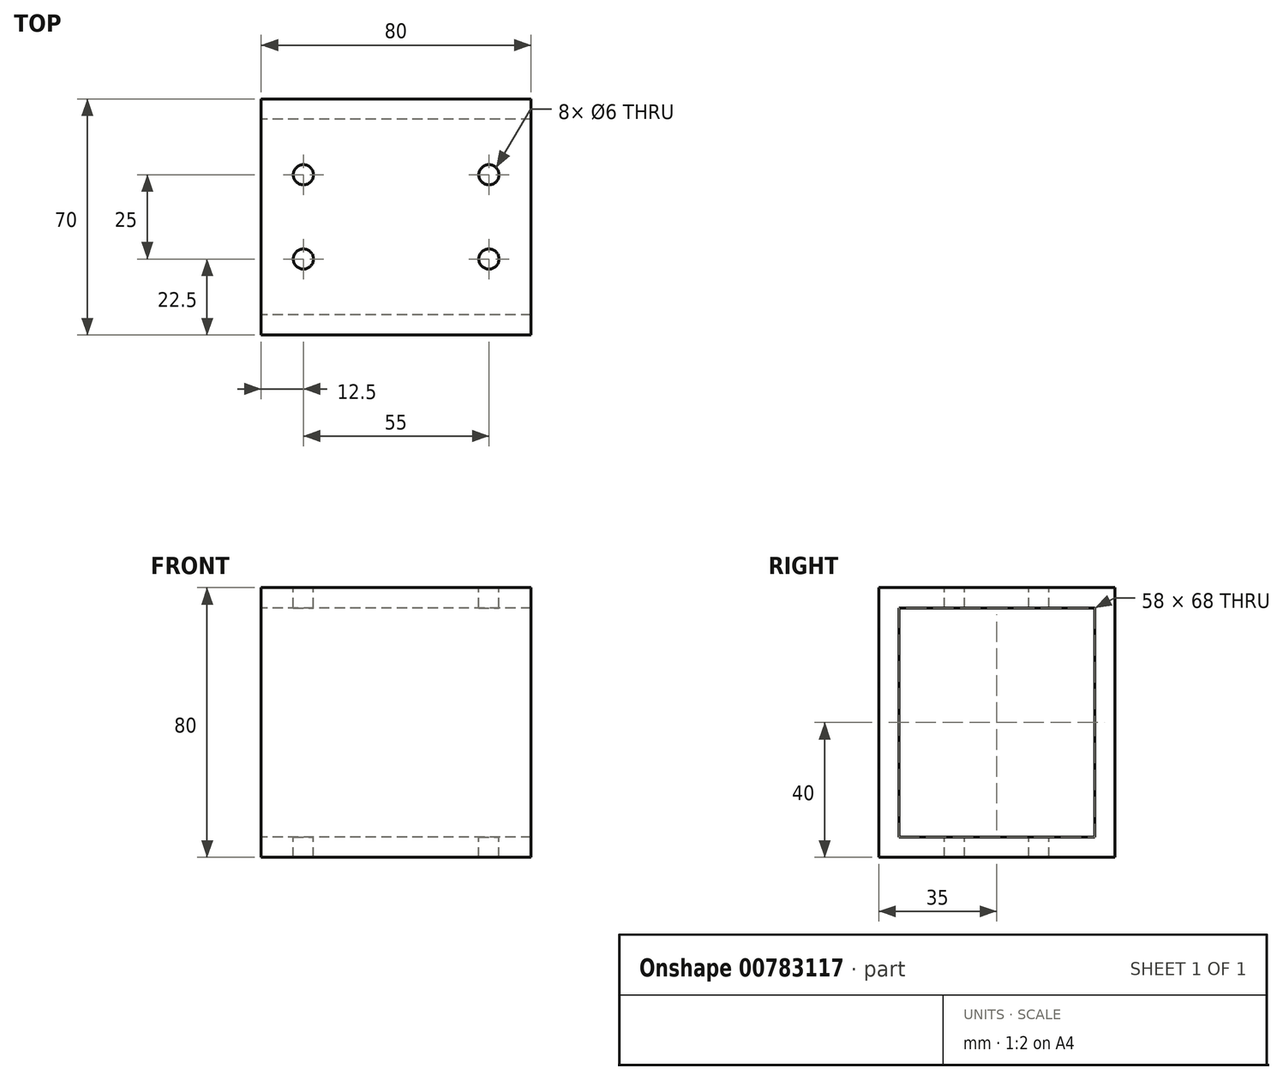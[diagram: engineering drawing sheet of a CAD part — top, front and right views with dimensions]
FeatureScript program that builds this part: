
annotation { "Feature Type Name" : "Feature", "Feature Type Description" : "" }
export const myFeature = defineFeature(function(context is Context, id is Id, definition is map)
    precondition{}
    {
        {
            var Q0;
            Q0=qCreatedBy(makeId("Right.planeOp"),FACE);
            var sketch = newSketch(context, id + "F0", { "sketchPlane" : qUnion([Q0])});
            skLineSegment(sketch, "E0.bottom", {"start": v(0, 0) * mm, "end": v(-70, 0) * mm});
            skLineSegment(sketch, "E0.top", {"start": v(0, 80) * mm, "end": v(-70, 80) * mm});
            skLineSegment(sketch, "E0.left", {"start": v(0, 0) * mm, "end": v(0, 80) * mm});
            skLineSegment(sketch, "E0.right", {"start": v(-70, 0) * mm, "end": v(-70, 80) * mm});
            skLineSegment(sketch, "E1.0", {"start": v(-6, 74) * mm, "end": v(-64, 74) * mm});
            skLineSegment(sketch, "E1.1", {"start": v(-6, 6) * mm, "end": v(-6, 74) * mm});
            skLineSegment(sketch, "E1.2", {"start": v(-6, 6) * mm, "end": v(-64, 6) * mm});
            skLineSegment(sketch, "E1.3", {"start": v(-64, 6) * mm, "end": v(-64, 74) * mm});
            skSolve(sketch);
        }
        {
            var Q0;
            Q0=makeQuery(id+"F0.imprint","IMPRINT",FACE,{"disambiguationData":[TD([[makeQuery(id+"F0.imprint","IMPRINT",EDGE,{"derivedFrom":sQuery(id+"F0.wireOp",EDGE,"E0.bottom")}),-1.0]])]});
            extrude(context, id + "F1", {"entities" : qUnion([Q0]), "depth" : 80 * mm, "offsetDistance" : 25 * mm});
        }
        {
            var Q0;
            Q0=makeQuery(id+"F1.opExtrude","SWEPT_FACE",FACE,{"disambiguationData":[OSD([sQuery(id+"F0.wireOp",EDGE,"E0.top")])]});
            var sketch = newSketch(context, id + "F2", { "sketchPlane" : qUnion([Q0])});
            skCircle(sketch, "E2", {"center": v(12.5, -22.5) * mm, "radius": 2.05 * mm});
            skCircle(sketch, "E3", {"center": v(67.5, -22.5) * mm, "radius": 2.05 * mm});
            skCircle(sketch, "E4", {"center": v(12.5, -47.5) * mm, "radius": 3.8 * mm});
            skCircle(sketch, "E5", {"center": v(67.5, -47.5) * mm, "radius": 2.54 * mm});
            skSolve(sketch);
        }
        {
            var Q0;
            Q0=sQuery(id+"F2.wireOp",VERTEX,"E2.center");
            var Q1;
            Q1=sQuery(id+"F2.wireOp",VERTEX,"E3.center");
            var Q2;
            Q2=sQuery(id+"F2.wireOp",VERTEX,"E5.center");
            var Q3;
            Q3=sQuery(id+"F2.wireOp",VERTEX,"E4.center");
            var Q4;
            Q4=makeQuery(id+"F1.opExtrude","SWEPT_BODY",BODY,{"disambiguationData":[OSD([sQuery(id+"F0.wireOp",EDGE,"E0.bottom"),sQuery(id+"F0.wireOp",EDGE,"E0.top"),sQuery(id+"F0.wireOp",EDGE,"E0.left"),sQuery(id+"F0.wireOp",EDGE,"E0.right"),sQuery(id+"F0.wireOp",EDGE,"E1.0"),sQuery(id+"F0.wireOp",EDGE,"E1.1"),sQuery(id+"F0.wireOp",EDGE,"E1.2"),sQuery(id+"F0.wireOp",EDGE,"E1.3")])]});
            hole(context, id + "F3", {"style" : HoleStyle.SIMPLE, "endStyle" : HoleEndStyle.THROUGH, "holeDiameter" : 6 * mm, "majorDiameter" : 5 * mm, "isTappedThrough" : true, "tappedDepth" : 12 * mm, "tapClearance" : 3, "locations" : qUnion([Q0, Q1, Q2, Q3]), "scope" : qUnion([Q4])});
        }
    });
